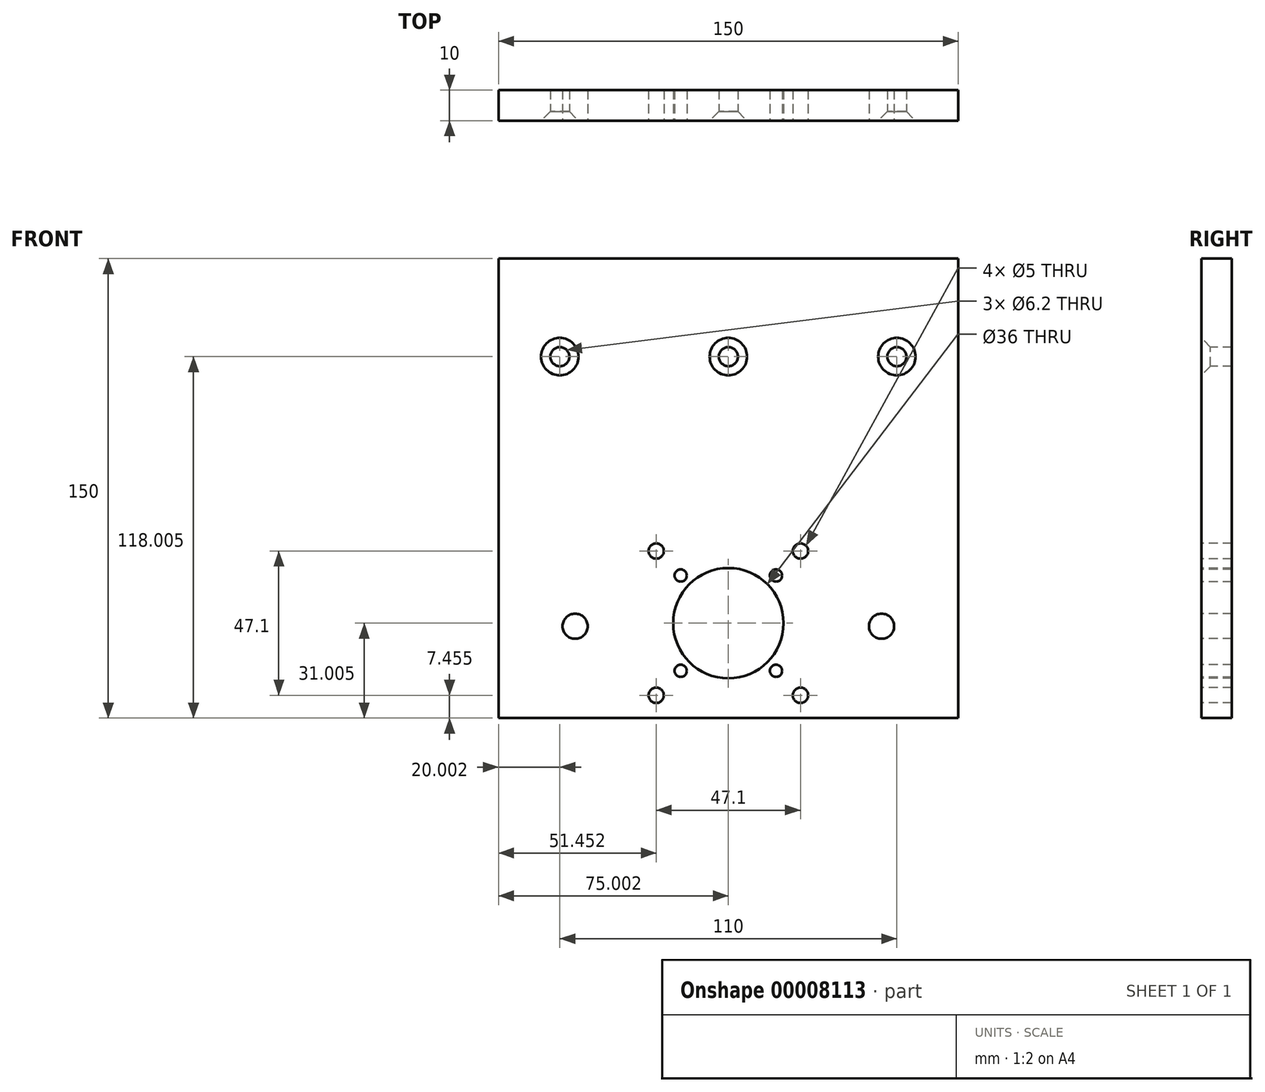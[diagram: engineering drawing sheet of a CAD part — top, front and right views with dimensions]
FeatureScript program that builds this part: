
annotation { "Feature Type Name" : "Feature", "Feature Type Description" : "" }
export const myFeature = defineFeature(function(context is Context, id is Id, definition is map)
    precondition{}
    {
        {
            var Q0;
            Q0=qCreatedBy(makeId("Front.planeOp"),FACE);
            var sketch = newSketch(context, id + "F0", { "sketchPlane" : qUnion([Q0])});
            skLineSegment(sketch, "E0", {"start": v(-95.98, -36.32) * mm, "end": v(54.02, -36.32) * mm});
            skLineSegment(sketch, "E1", {"start": v(54.02, -36.32) * mm, "end": v(54.02, 113.68) * mm});
            skLineSegment(sketch, "E2", {"start": v(54.02, 113.68) * mm, "end": v(-95.98, 113.68) * mm});
            skLineSegment(sketch, "E3", {"start": v(-95.98, 113.68) * mm, "end": v(-95.98, -36.32) * mm});
            skCircle(sketch, "E4", {"center": v(-75.98, 81.68) * mm, "radius": 3.1 * mm});
            skCircle(sketch, "E5", {"center": v(-20.98, 81.68) * mm, "radius": 3.1 * mm});
            skCircle(sketch, "E6", {"center": v(34.02, 81.68) * mm, "radius": 3.1 * mm});
            skCircle(sketch, "E7", {"center": v(-70.98, -6.32) * mm, "radius": 4.1 * mm});
            skCircle(sketch, "E8", {"center": v(29.02, -6.32) * mm, "radius": 4.1 * mm});
            skCircle(sketch, "E9", {"center": v(-20.98, -5.32) * mm, "radius": 18 * mm});
            skCircle(sketch, "E10", {"center": v(-44.53, 18.23) * mm, "radius": 2.5 * mm});
            skCircle(sketch, "E11", {"center": v(2.57, 18.23) * mm, "radius": 2.5 * mm});
            skCircle(sketch, "E12", {"center": v(2.57, -28.87) * mm, "radius": 2.5 * mm});
            skCircle(sketch, "E13", {"center": v(-44.53, -28.87) * mm, "radius": 2.5 * mm});
            skCircle(sketch, "E14", {"center": v(-36.53, -20.87) * mm, "radius": 2 * mm});
            skCircle(sketch, "E15", {"center": v(-36.53, 10.24) * mm, "radius": 2 * mm});
            skCircle(sketch, "E16", {"center": v(-5.42, 10.24) * mm, "radius": 2 * mm});
            skCircle(sketch, "E17", {"center": v(-5.42, -20.87) * mm, "radius": 2 * mm});
            skSolve(sketch);
        }
        {
            var Q0;
            Q0=makeQuery(id+"F0.imprint","IMPRINT",FACE,{"disambiguationData":[TD([[makeQuery(id+"F0.imprint","IMPRINT",EDGE,{"derivedFrom":sQuery(id+"F0.wireOp",EDGE,"E0")}),1.0]])]});
            extrude(context, id + "F1", {"entities" : qUnion([Q0]), "oppositeDirection" : true, "depth" : 10 * mm});
        }
        {
            var Q0;
            Q0=makeQuery(id+"F1.opExtrude","CAP_EDGE",EDGE,{"disambiguationData":[OSD([sQuery(id+"F0.wireOp",EDGE,"E4")])],"isStart":true});
            var Q1;
            Q1=makeQuery(id+"F1.opExtrude","CAP_EDGE",EDGE,{"disambiguationData":[OSD([sQuery(id+"F0.wireOp",EDGE,"E5")])],"isStart":true});
            var Q2;
            Q2=makeQuery(id+"F1.opExtrude","CAP_EDGE",EDGE,{"disambiguationData":[OSD([sQuery(id+"F0.wireOp",EDGE,"E6")])],"isStart":true});
            chamfer(context, id + "F2", {"entities" : qUnion([Q0, Q1, Q2]), "width" : 3 * mm, "tangentPropagation" : true});
        }
    });
